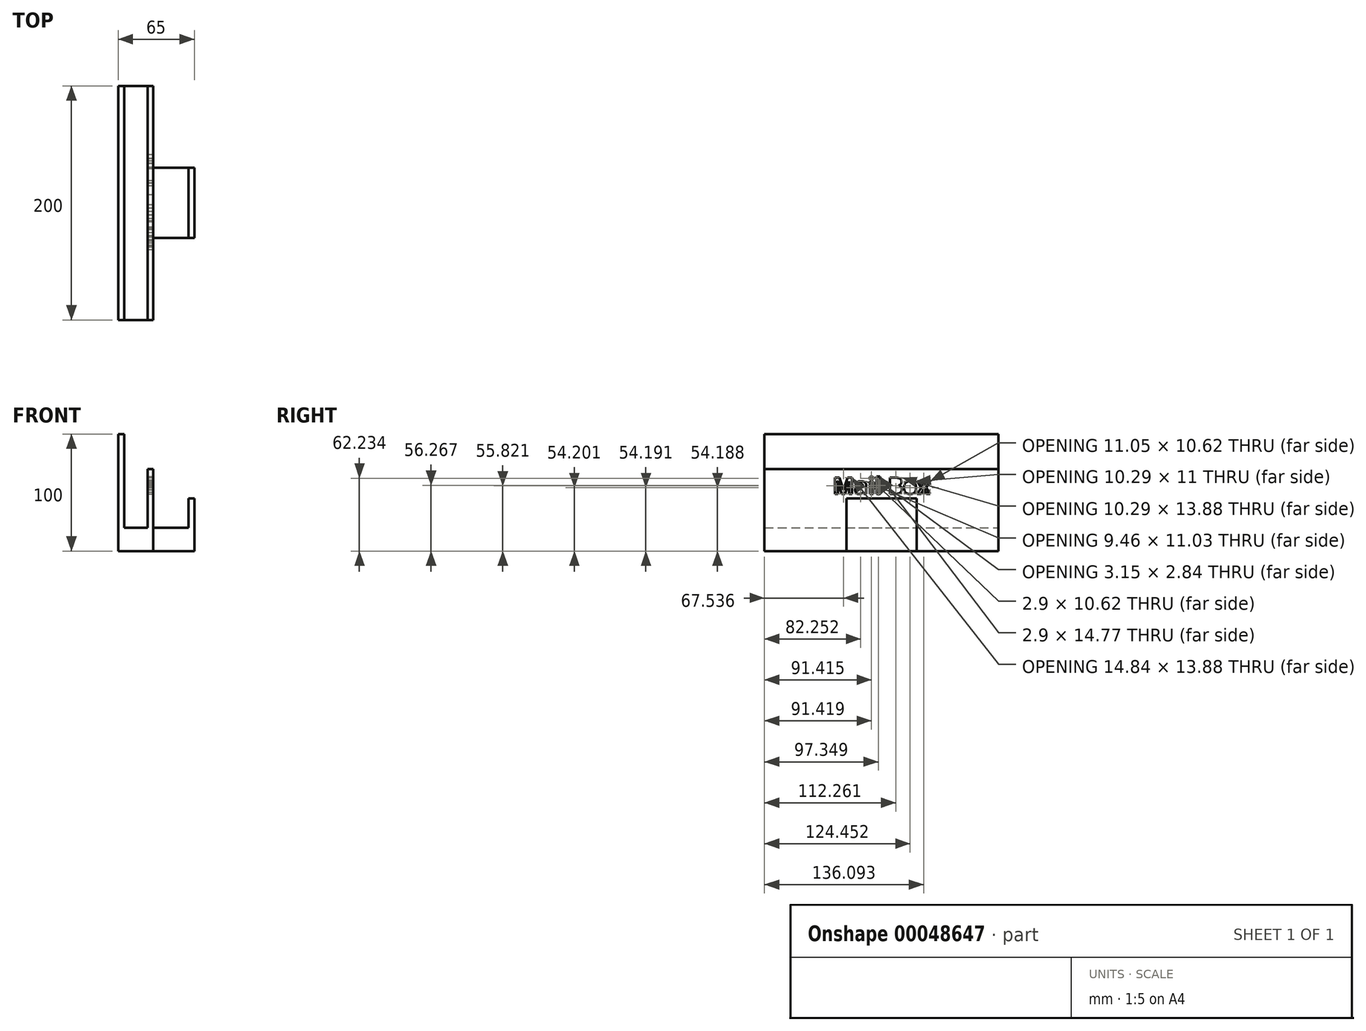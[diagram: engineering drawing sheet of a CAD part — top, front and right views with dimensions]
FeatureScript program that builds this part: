
annotation { "Feature Type Name" : "Feature", "Feature Type Description" : "" }
export const myFeature = defineFeature(function(context is Context, id is Id, definition is map)
    precondition{}
    {
        {
            assignVariable(context, id + "F0", {"name" : "largura", "anyValue" : 200});
        }
        {
            var Q0;
            Q0=qCreatedBy(makeId("Front.planeOp"),FACE);
            var sketch = newSketch(context, id + "F1", { "sketchPlane" : qUnion([Q0])});
            skLineSegment(sketch, "E0", {"start": v(-31.83, 100) * mm, "end": v(-31.83, 0) * mm});
            skLineSegment(sketch, "E1", {"start": v(33.17, 0) * mm, "end": v(33.17, 45) * mm});
            skLineSegment(sketch, "E2", {"start": v(33.17, 45) * mm, "end": v(28.17, 45) * mm});
            skLineSegment(sketch, "E3", {"start": v(28.17, 45) * mm, "end": v(28.17, 20) * mm});
            skLineSegment(sketch, "E4", {"start": v(-26.83, 20) * mm, "end": v(-26.83, 100) * mm});
            skLineSegment(sketch, "E5", {"start": v(-31.83, 100) * mm, "end": v(-26.83, 100) * mm});
            skLineSegment(sketch, "E6", {"start": v(-31.83, 0) * mm, "end": v(33.17, 0) * mm});
            skLineSegment(sketch, "E7", {"start": v(-26.83, 20) * mm, "end": v(-6.83, 20) * mm});
            skLineSegment(sketch, "E8", {"start": v(-6.83, 20) * mm, "end": v(-6.83, 70) * mm});
            skLineSegment(sketch, "E9", {"start": v(-1.83, 70) * mm, "end": v(-1.83, 20) * mm});
            skLineSegment(sketch, "E10", {"start": v(-1.83, 20) * mm, "end": v(28.17, 20) * mm});
            skLineSegment(sketch, "E11", {"start": v(-6.83, 70) * mm, "end": v(-1.83, 70) * mm});
            skSolve(sketch);
        }
        {
            var Q0;
            Q0=makeQuery(id+"F1.imprint","IMPRINT",FACE,{"disambiguationData":[TD([[makeQuery(id+"F1.imprint","IMPRINT",EDGE,{"derivedFrom":sQuery(id+"F1.wireOp",EDGE,"E0")}),1.0]])]});
            extrude(context, id + "F2", {"entities" : qUnion([Q0]), "depth" : (getVariable(context, 'largura')) * mm});
        }
        {
            var Q0;
            Q0=qCreatedBy(makeId("Front.planeOp"),FACE);
            var sketch = newSketch(context, id + "F3", { "sketchPlane" : qUnion([Q0])});
            skLineSegment(sketch, "E12", {"start": v(-1.83, 56.24) * mm, "end": v(-1.83, -3.94) * mm});
            skLineSegment(sketch, "E13", {"start": v(-1.83, 56.24) * mm, "end": v(38.25, 56.24) * mm});
            skLineSegment(sketch, "E14", {"start": v(38.25, 56.24) * mm, "end": v(38.25, -3.94) * mm});
            skLineSegment(sketch, "E15", {"start": v(38.25, -3.94) * mm, "end": v(-1.83, -3.94) * mm});
            skSolve(sketch);
        }
        {
            var Q0;
            Q0 = qSketchRegion(id + "F3", true);
            extrude(context, id + "F4", {"entities" : qUnion([Q0]), "depth" : 70 * mm});
        }
        {
            var Q0;
            Q0=makeQuery(id+"F2.opExtrude","CAP_FACE",FACE,{"disambiguationData":[OSD([sQuery(id+"F1.wireOp",EDGE,"E0"),sQuery(id+"F1.wireOp",EDGE,"E1"),sQuery(id+"F1.wireOp",EDGE,"E2"),sQuery(id+"F1.wireOp",EDGE,"E3"),sQuery(id+"F1.wireOp",EDGE,"E4"),sQuery(id+"F1.wireOp",EDGE,"E5"),sQuery(id+"F1.wireOp",EDGE,"E6"),sQuery(id+"F1.wireOp",EDGE,"E7"),sQuery(id+"F1.wireOp",EDGE,"E8"),sQuery(id+"F1.wireOp",EDGE,"E9"),sQuery(id+"F1.wireOp",EDGE,"E10"),sQuery(id+"F1.wireOp",EDGE,"E11")])],"isStart":false});
            cPlane(context, id + "F5", {"entities" : qUnion([Q0]), "cplaneType" : CPlaneType.OFFSET, "offset" : (getVariable(context, 'largura') / 2) * mm, "oppositeDirection" : true, "width" : 150 * mm, "height" : 150 * mm});
        }
        {
            var Q0;
            Q0=makeQuery(id+"F4.opExtrude","SWEPT_BODY",BODY,{"disambiguationData":[OSD([sQuery(id+"F3.wireOp",EDGE,"E12"),sQuery(id+"F3.wireOp",EDGE,"E13"),sQuery(id+"F3.wireOp",EDGE,"E14"),sQuery(id+"F3.wireOp",EDGE,"E15")])]});
            var Q1;
            Q1=qCreatedBy(id+"F5.planeOp",FACE);
            mirror(context, id + "F6", {"entities" : qUnion([Q0]), "mirrorPlane" : qUnion([Q1])});
        }
        {
            var Q0;
            Q0=makeQuery(id+"F6.opPattern","COPY",BODY,{"derivedFrom":makeQuery(id+"F4.opExtrude","SWEPT_BODY",BODY,{"disambiguationData":[OSD([sQuery(id+"F3.wireOp",EDGE,"E12"),sQuery(id+"F3.wireOp",EDGE,"E13"),sQuery(id+"F3.wireOp",EDGE,"E14"),sQuery(id+"F3.wireOp",EDGE,"E15")])]}),"instanceName":"1"});
            var Q1;
            Q1=makeQuery(id+"F4.opExtrude","SWEPT_BODY",BODY,{"disambiguationData":[OSD([sQuery(id+"F3.wireOp",EDGE,"E12"),sQuery(id+"F3.wireOp",EDGE,"E13"),sQuery(id+"F3.wireOp",EDGE,"E14"),sQuery(id+"F3.wireOp",EDGE,"E15")])]});
            var Q2;
            Q2=makeQuery(id+"F2.opExtrude","SWEPT_BODY",BODY,{"disambiguationData":[OSD([sQuery(id+"F1.wireOp",EDGE,"E0"),sQuery(id+"F1.wireOp",EDGE,"E1"),sQuery(id+"F1.wireOp",EDGE,"E2"),sQuery(id+"F1.wireOp",EDGE,"E3"),sQuery(id+"F1.wireOp",EDGE,"E4"),sQuery(id+"F1.wireOp",EDGE,"E5"),sQuery(id+"F1.wireOp",EDGE,"E6"),sQuery(id+"F1.wireOp",EDGE,"E7"),sQuery(id+"F1.wireOp",EDGE,"E8"),sQuery(id+"F1.wireOp",EDGE,"E9"),sQuery(id+"F1.wireOp",EDGE,"E10"),sQuery(id+"F1.wireOp",EDGE,"E11")])]});
            booleanBodies(context, id + "F7", {"operationType" : BooleanOperationType.SUBTRACTION, "tools" : qUnion([Q0, Q1]), "targets" : qUnion([Q2])});
        }
        {
            var Q0;
            {var subQ0=makeQuery(id+"F4.opExtrude","SWEPT_FACE",FACE,{"disambiguationData":[OSD([sQuery(id+"F3.wireOp",EDGE,"E12")])]});Q0=makeQuery(id+"F7.opBoolean","MERGE",FACE,{"derivedFrom":[makeQuery(id+"F2.opExtrude","SWEPT_FACE",FACE,{"disambiguationData":[OSD([sQuery(id+"F1.wireOp",EDGE,"E9")])]}),subQ0,makeQuery(id+"F6.opPattern","COPY",FACE,{"derivedFrom":subQ0,"instanceName":"1"})]});}
            var sketch = newSketch(context, id + "F8", { "sketchPlane" : qUnion([Q0])});
            skText(sketch, "E16", { "text": "Mail Box", "fontName": "OpenSans-Bold.ttf"});
            const initialGuessF8  = {"E16": [-0.14163, 0.04888, 1, 0, 0.014]};
            skSetInitialGuess(sketch, initialGuessF8);
            skSolve(sketch);
        }
        {
            var Q0;
            Q0=makeQuery(id+"F8.imprint","IMPRINT",FACE,{"disambiguationData":[TD([[makeQuery(id+"F8.imprint","IMPRINT",EDGE,{"derivedFrom":sQuery(id+"F8.wireOp",EDGE,"E16.sketch_text.stroke-0")}),-1.0]])]});
            var Q1;
            Q1=makeQuery(id+"F8.imprint","IMPRINT",FACE,{"disambiguationData":[TD([[makeQuery(id+"F8.imprint","IMPRINT",EDGE,{"derivedFrom":sQuery(id+"F8.wireOp",EDGE,"E16.sketch_text.stroke-37")}),1.0]])]});
            var Q2;
            Q2=makeQuery(id+"F8.imprint","IMPRINT",FACE,{"disambiguationData":[TD([[makeQuery(id+"F8.imprint","IMPRINT",EDGE,{"derivedFrom":sQuery(id+"F8.wireOp",EDGE,"E16.sketch_text.stroke-44")}),-1.0]])]});
            var Q3;
            Q3=makeQuery(id+"F8.imprint","IMPRINT",FACE,{"disambiguationData":[TD([[makeQuery(id+"F8.imprint","IMPRINT",EDGE,{"derivedFrom":sQuery(id+"F8.wireOp",EDGE,"E16.sketch_text.stroke-49")}),-1.0]])]});
            var Q4;
            Q4=makeQuery(id+"F8.imprint","IMPRINT",FACE,{"disambiguationData":[TD([[makeQuery(id+"F8.imprint","IMPRINT",EDGE,{"derivedFrom":sQuery(id+"F8.wireOp",EDGE,"E16.sketch_text.stroke-53")}),-1.0]])]});
            var Q5;
            Q5=makeQuery(id+"F8.imprint","IMPRINT",FACE,{"disambiguationData":[TD([[makeQuery(id+"F8.imprint","IMPRINT",EDGE,{"derivedFrom":sQuery(id+"F8.wireOp",EDGE,"E16.sketch_text.stroke-69")}),1.0]])]});
            var Q6;
            Q6=makeQuery(id+"F8.imprint","IMPRINT",FACE,{"disambiguationData":[TD([[makeQuery(id+"F8.imprint","IMPRINT",EDGE,{"derivedFrom":sQuery(id+"F8.wireOp",EDGE,"E16.sketch_text.stroke-76")}),1.0]])]});
            var Q7;
            Q7=makeQuery(id+"F8.imprint","IMPRINT",FACE,{"disambiguationData":[TD([[makeQuery(id+"F8.imprint","IMPRINT",EDGE,{"derivedFrom":sQuery(id+"F8.wireOp",EDGE,"E16.sketch_text.stroke-82")}),1.0]])]});
            var Q8;
            Q8=makeQuery(id+"F8.imprint","IMPRINT",FACE,{"disambiguationData":[TD([[makeQuery(id+"F8.imprint","IMPRINT",EDGE,{"derivedFrom":sQuery(id+"F8.wireOp",EDGE,"E16.sketch_text.stroke-100")}),-1.0]])]});
            var Q9;
            Q9=makeQuery(id+"F8.imprint","IMPRINT",FACE,{"disambiguationData":[TD([[makeQuery(id+"F8.imprint","IMPRINT",EDGE,{"derivedFrom":sQuery(id+"F8.wireOp",EDGE,"E16.sketch_text.stroke-19")}),-1.0]])]});
            var Q10;
            Q10=makeQuery(id+"F8.imprint","IMPRINT",FACE,{"disambiguationData":[TD([[makeQuery(id+"F8.imprint","IMPRINT",EDGE,{"derivedFrom":sQuery(id+"F8.wireOp",EDGE,"E16.sketch_text.stroke-82")}),-1.0]])]});
            var Q11;
            Q11=makeQuery(id+"F8.imprint","IMPRINT",FACE,{"disambiguationData":[TD([[makeQuery(id+"F8.imprint","IMPRINT",EDGE,{"derivedFrom":sQuery(id+"F8.wireOp",EDGE,"E16.sketch_text.stroke-57")}),-1.0]])]});
            var Q12;
            Q12 = qSketchRegion(id + "F8", true);
            extrude(context, id + "F9", {"entities" : qUnion([Q0, Q1, Q2, Q3, Q4, Q5, Q6, Q7, Q8, Q9, Q10, Q11, Q12]), "operationType" : NewBodyOperationType.REMOVE, "oppositeDirection" : true, "depth" : 5 * mm});
        }
    });
